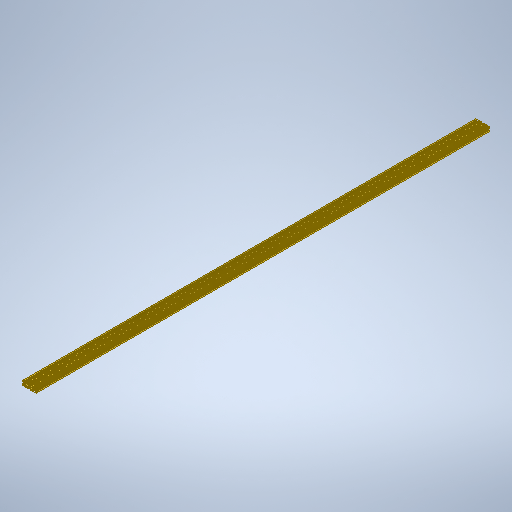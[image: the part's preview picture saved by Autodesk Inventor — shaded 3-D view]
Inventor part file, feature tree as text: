
AUTODESK INVENTOR PART (.ipt)
format: ipt  version: 2025.2 (Build 292293000, 293)  size: 506,368 bytes
history: native  units: mm
features: mirror x2, fillet x2, extrude x1, sketch x1
ambient origin geometry x8: Origin, YZ Plane, XZ Plane, XY Plane, X Axis, Y Axis, Z Axis, Center Point
bodies: Body1 (feature_tree)
feature tree (6):
  extrude  "Extrusão2"  Depth=60.0mm
  mirror  "Espelhar5"
  mirror  "Espelhar6"
  fillet  "Arredondamento3"  Radius=20.0mm
  fillet  "Arredondamento4"  Radius=6.2mm
  sketch  "Esboço2"  dims[d24=10.0mm d25=60.0mm d26=20.0mm d28=6.2mm d29=6.0mm d31=5.0mm d32=2.0mm d33=4.0mm d35=0.5mm d36=0.5mm d38=4.0mm d39=4.0mm d41=2000.0mm d42=0.0mm d43=1.0mm d44=1.0mm]
